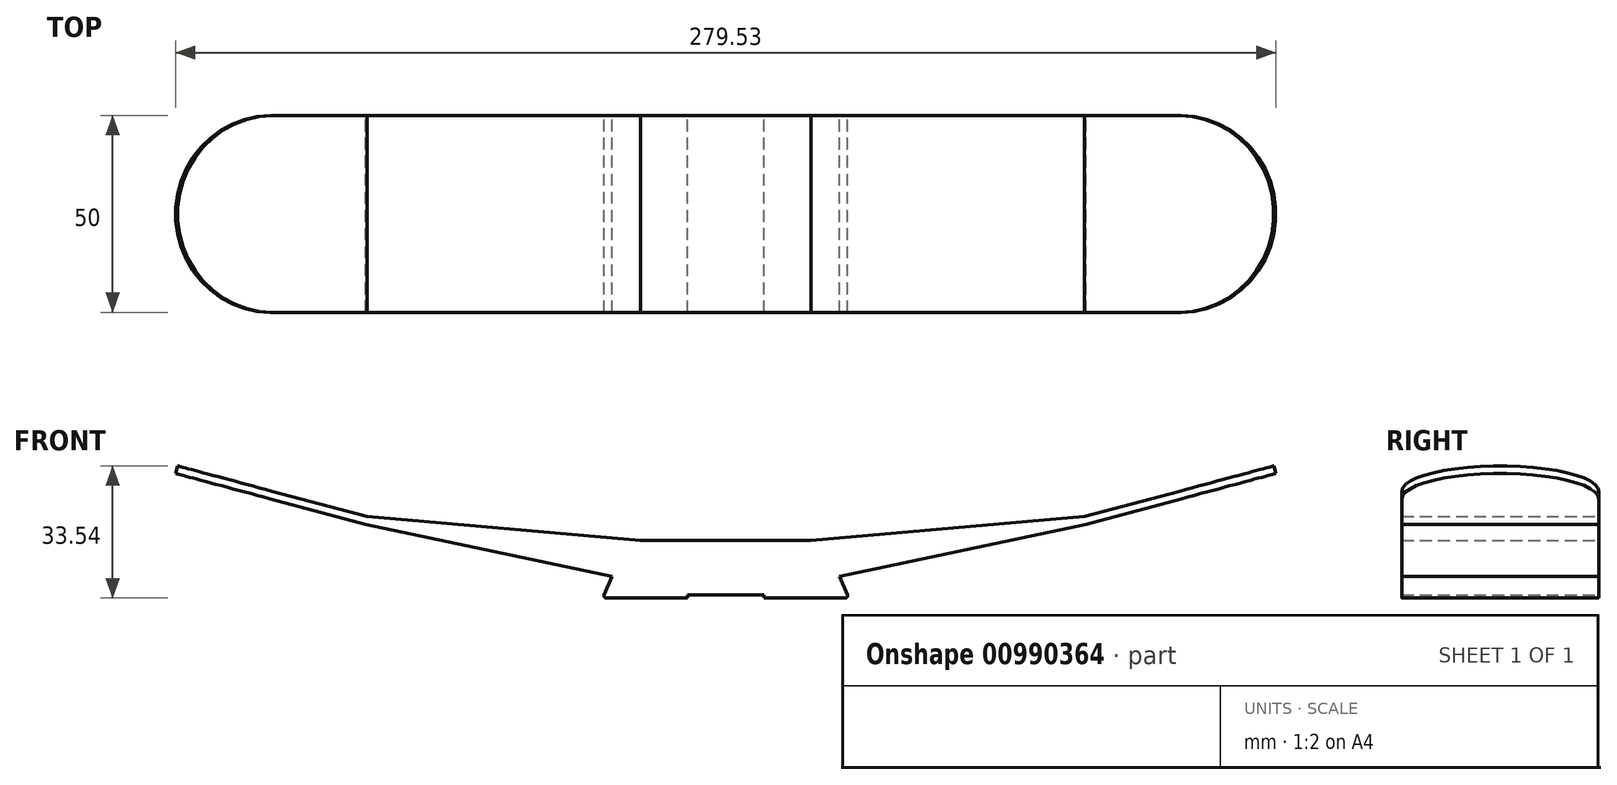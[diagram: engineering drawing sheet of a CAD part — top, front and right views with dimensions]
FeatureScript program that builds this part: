
annotation { "Feature Type Name" : "Feature", "Feature Type Description" : "" }
export const myFeature = defineFeature(function(context is Context, id is Id, definition is map)
    precondition{}
    {
        {
            var Q0;
            Q0=qCreatedBy(makeId("Front.planeOp"),FACE);
            var sketch = newSketch(context, id + "F0", { "sketchPlane" : qUnion([Q0])});
            skLineSegment(sketch, "E0", {"start": v(26.7, -11.58) * mm, "end": v(28.75, -6.78) * mm});
            skArc(sketch, "E1.filletArc", {"start": v(26.7, -11.58) * mm, "mid": v(26.74, -12.05) * mm, "end": v(27.15, -12.28) * mm});
            skLineSegment(sketch, "E2", {"start": v(27.15, -12.28) * mm, "end": v(47.85, -12.28) * mm});
            skLineSegment(sketch, "E3", {"start": v(47.85, -12.28) * mm, "end": v(47.85, -11.48) * mm});
            skLineSegment(sketch, "E4", {"start": v(28.75, -6.78) * mm, "end": v(35.82, 0.3) * mm});
            skLineSegment(sketch, "E5", {"start": v(35.82, 0.3) * mm, "end": v(-33.92, 6.4) * mm});
            skLineSegment(sketch, "E6", {"start": v(-33.92, 6.4) * mm, "end": v(-82.21, 19.34) * mm});
            skLineSegment(sketch, "E7.0", {"start": v(-33.57, 8.37) * mm, "end": v(-81.7, 21.27) * mm});
            skLineSegment(sketch, "E7.4", {"start": v(35.9, 2.3) * mm, "end": v(-33.57, 8.37) * mm});
            skArc(sketch, "E8", {"start": v(-81.7, 21.27) * mm, "mid": v(-82.92, 20.56) * mm, "end": v(-82.21, 19.34) * mm});
            skLineSegment(sketch, "E9", {"start": v(47.85, -11.48) * mm, "end": v(57.6, -11.48) * mm});
            skLineSegment(sketch, "E10", {"start": v(35.9, 2.3) * mm, "end": v(57.6, 2.3) * mm});
            skLineSegment(sketch, "E11", {"start": v(57.6, 2.3) * mm, "end": v(57.6, -11.48) * mm});
            skLineSegment(sketch, "E12", {"start": v(28.75, -6.78) * mm, "end": v(-33.92, 6.4) * mm});
            skSolve(sketch);
        }
        {
            var Q0;
            Q0=makeQuery(id+"F0.imprint","IMPRINT",FACE,{"disambiguationData":[TD([[makeQuery(id+"F0.imprint","IMPRINT",EDGE,{"derivedFrom":sQuery(id+"F0.wireOp",EDGE,"E0")}),-1.0]])]});
            var Q1;
            Q1=makeQuery(id+"F0.imprint","IMPRINT",FACE,{"disambiguationData":[TD([[makeQuery(id+"F0.imprint","IMPRINT",EDGE,{"derivedFrom":sQuery(id+"F0.wireOp",EDGE,"E4")}),1.0]])]});
            extrude(context, id + "F1", {"entities" : qUnion([Q0, Q1]), "depth" : 50 * mm, "offsetDistance" : 25 * mm});
        }
        {
            var Q0;
            Q0=makeQuery(id+"F1.opExtrude","SWEPT_FACE",FACE,{"disambiguationData":[OSD([sQuery(id+"F0.wireOp",EDGE,"E7.0")])]});
            var sketch = newSketch(context, id + "F2", { "sketchPlane" : qUnion([Q0])});
            skLineSegment(sketch, "E13", {"start": v(-59.5, -50) * mm, "end": v(-110.21, -50) * mm});
            skLineSegment(sketch, "E14", {"start": v(-110.21, -50) * mm, "end": v(-110.21, 0) * mm});
            skLineSegment(sketch, "E15", {"start": v(-110.21, 0) * mm, "end": v(-59.5, 0) * mm});
            skArc(sketch, "E16", {"start": v(-59.5, 0) * mm, "mid": v(-84.37, -25) * mm, "end": v(-59.5, -50) * mm});
            skSolve(sketch);
        }
        {
            var Q0;
            {var subQ3=sQuery(id+"F2.wireOp",EDGE,"E16");Q0=makeQuery(id+"F2.imprint","IMPRINT",FACE,{"disambiguationData":[TD([[makeQuery(id+"F2.imprint","IMPRINT",EDGE,{"derivedFrom":subQ3}),-1.0]])]});}
            var Q1;
            {var subQ2=sQuery(id+"F2.wireOp",EDGE,"E14");Q1=makeQuery(id+"F2.imprint","IMPRINT",FACE,{"disambiguationData":[TD([[makeQuery(id+"F2.imprint","IMPRINT",EDGE,{"derivedFrom":subQ2}),-1.0]])]});}
            extrude(context, id + "F3", {"entities" : qUnion([Q0, Q1]), "operationType" : NewBodyOperationType.REMOVE, "oppositeDirection" : true, "depth" : 9.8 * mm, "offsetDistance" : 25 * mm});
        }
        {
            var Q0;
            Q0=makeQuery(id+"F1.opExtrude","SWEPT_BODY",BODY,{"disambiguationData":[OSD([sQuery(id+"F0.wireOp",EDGE,"E0"),sQuery(id+"F0.wireOp",EDGE,"E1.filletArc"),sQuery(id+"F0.wireOp",EDGE,"E2"),sQuery(id+"F0.wireOp",EDGE,"E3"),sQuery(id+"F0.wireOp",EDGE,"E6"),sQuery(id+"F0.wireOp",EDGE,"E7.0"),sQuery(id+"F0.wireOp",EDGE,"E7.4"),sQuery(id+"F0.wireOp",EDGE,"E8"),sQuery(id+"F0.wireOp",EDGE,"E9"),sQuery(id+"F0.wireOp",EDGE,"E10"),sQuery(id+"F0.wireOp",EDGE,"E11"),sQuery(id+"F0.wireOp",EDGE,"E12")])]});
            var Q1;
            Q1=makeQuery(id+"F1.opExtrude","SWEPT_FACE",FACE,{"disambiguationData":[OSD([sQuery(id+"F0.wireOp",EDGE,"E11")])]});
            mirror(context, id + "F4", {"operationType" : NewBodyOperationType.ADD, "entities" : qUnion([Q0]), "mirrorPlane" : qUnion([Q1])});
        }
    });
